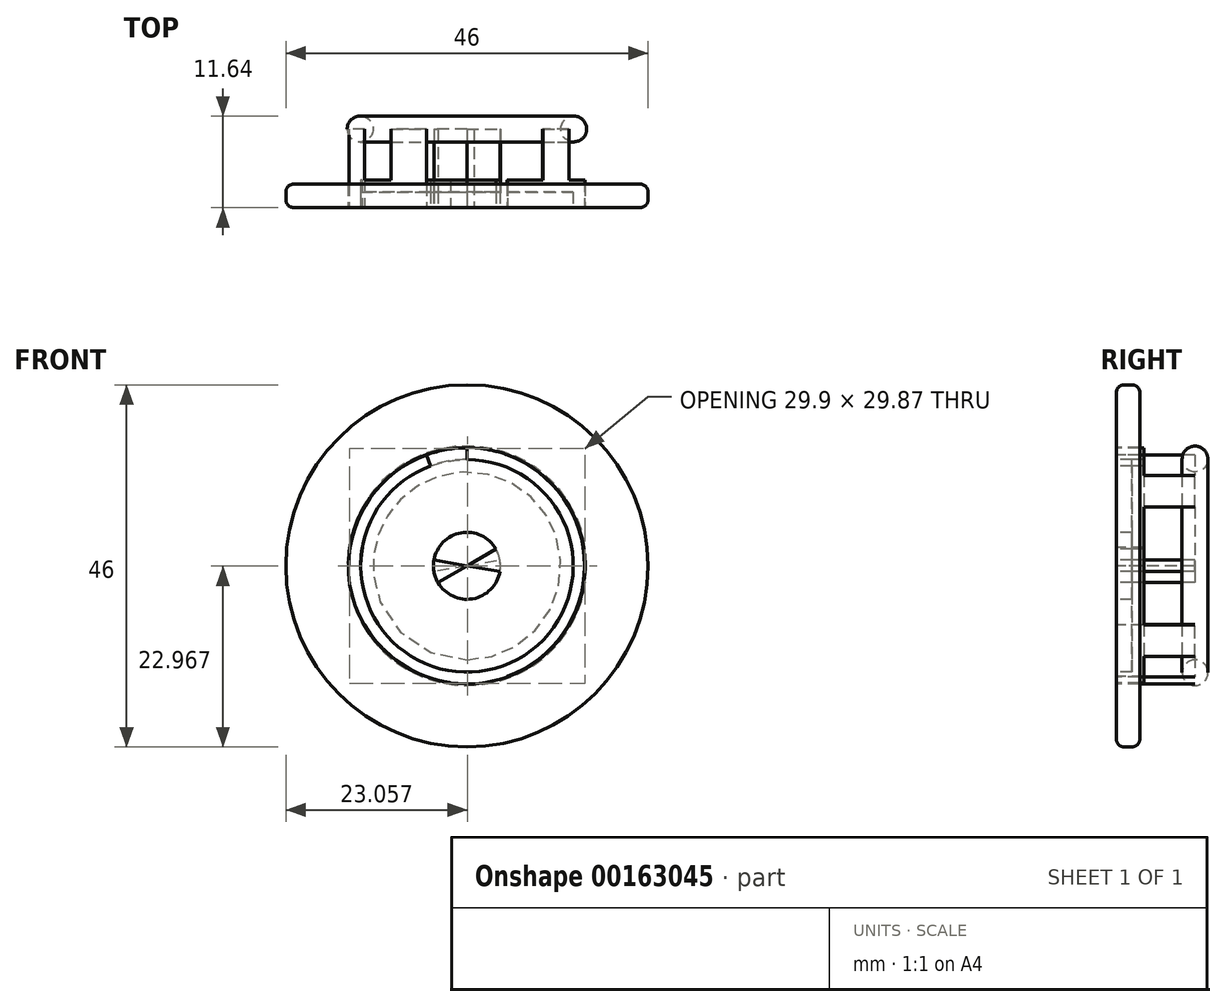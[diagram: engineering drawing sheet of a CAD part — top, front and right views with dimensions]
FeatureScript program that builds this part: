
annotation { "Feature Type Name" : "Feature", "Feature Type Description" : "" }
export const myFeature = defineFeature(function(context is Context, id is Id, definition is map)
    precondition{}
    {
        {
            var Q0;
            Q0=qCreatedBy(makeId("Front.planeOp"),FACE);
            var sketch = newSketch(context, id + "F0", { "sketchPlane" : qUnion([Q0])});
            skCircle(sketch, "E0", {"center": v(0, 0) * mm, "radius": 15 * mm});
            skCircle(sketch, "E1", {"center": v(0, 0) * mm, "radius": 4.25 * mm});
            skCircle(sketch, "E2", {"center": v(0, 0) * mm, "radius": 23 * mm});
            skCircle(sketch, "E3", {"center": v(0, 0) * mm, "radius": 13.5 * mm});
            skLineSegment(sketch, "E4", {"start": v(0, 0) * mm, "end": v(0, 15) * mm});
            skLineSegment(sketch, "E5.1.0", {"start": v(0, 0) * mm, "end": v(-5.13, 14.1) * mm});
            skLineSegment(sketch, "E5.2.0", {"start": v(0, 0) * mm, "end": v(-9.64, 11.5) * mm});
            skLineSegment(sketch, "E6.1.3.0", {"start": v(0, 0) * mm, "end": v(-13, 7.5) * mm});
            skArc(sketch, "E6.3.3.0", {"start": v(0, 13.5) * mm, "mid": v(-2.34, -13.3) * mm, "end": v(4.62, 12.69) * mm});
            skLineSegment(sketch, "E6.1.4.0", {"start": v(0, 0) * mm, "end": v(-14.77, 2.6) * mm});
            skArc(sketch, "E6.5.4.0", {"start": v(1.74, 14.9) * mm, "mid": v(-2.17, -14.84) * mm, "end": v(2.6, 14.77) * mm});
            skLineSegment(sketch, "E6.1.5.0", {"start": v(0, 0) * mm, "end": v(-14.77, -2.6) * mm});
            skArc(sketch, "E6.3.5.0", {"start": v(0, 13.5) * mm, "mid": v(-6.75, -11.7) * mm, "end": v(11.7, 6.75) * mm});
            skLineSegment(sketch, "E6.1.6.0", {"start": v(0, 0) * mm, "end": v(-13, -7.5) * mm});
            skLineSegment(sketch, "E6.1.7.0", {"start": v(0, 0) * mm, "end": v(-9.64, -11.5) * mm});
            skArc(sketch, "E6.3.7.0", {"start": v(0, 13.5) * mm, "mid": v(-2.34, -13.3) * mm, "end": v(4.62, 12.69) * mm});
            skArc(sketch, "E6.5.7.0", {"start": v(0, 15) * mm, "mid": v(-2.6, -14.77) * mm, "end": v(5.13, 14.1) * mm});
            skLineSegment(sketch, "E6.1.8.0", {"start": v(0, 0) * mm, "end": v(-5.13, -14.1) * mm});
            skLineSegment(sketch, "E7.1.9.0", {"start": v(0, 0) * mm, "end": v(0, -15) * mm});
            skLineSegment(sketch, "E7.1.10.0", {"start": v(0, 0) * mm, "end": v(5.13, -14.1) * mm});
            skArc(sketch, "E7.5.10.0", {"start": v(0, 15) * mm, "mid": v(-7.5, -13) * mm, "end": v(13, 7.5) * mm});
            skLineSegment(sketch, "E7.1.11.0", {"start": v(0, 0) * mm, "end": v(9.64, -11.5) * mm});
            skLineSegment(sketch, "E7.1.12.0", {"start": v(0, 0) * mm, "end": v(13, -7.5) * mm});
            skLineSegment(sketch, "E7.1.13.0", {"start": v(0, 0) * mm, "end": v(14.77, -2.6) * mm});
            skLineSegment(sketch, "E7.1.14.0", {"start": v(0, 0) * mm, "end": v(14.77, 2.6) * mm});
            skLineSegment(sketch, "E7.1.15.0", {"start": v(0, 0) * mm, "end": v(13, 7.5) * mm});
            skLineSegment(sketch, "E7.1.16.0", {"start": v(0, 0) * mm, "end": v(9.64, 11.5) * mm});
            skLineSegment(sketch, "E7.1.17.0", {"start": v(0, 0) * mm, "end": v(5.13, 14.1) * mm});
            skArc(sketch, "E8.trimOffspring", {"start": v(8.68, 10.34) * mm, "mid": v(6.75, 11.7) * mm, "end": v(4.62, 12.69) * mm});
            skArc(sketch, "E9.trimOffspring", {"start": v(9.64, 11.5) * mm, "mid": v(7.5, 13) * mm, "end": v(5.13, 14.1) * mm});
            skArc(sketch, "E10", {"start": v(1.74, 14.9) * mm, "mid": v(0.87, 14.97) * mm, "end": v(0, 15) * mm});
            skArc(sketch, "E11", {"start": v(5.13, 14.1) * mm, "mid": v(3.46, 14.6) * mm, "end": v(1.74, 14.9) * mm});
            skLineSegment(sketch, "E12", {"start": v(1.74, 14.9) * mm, "end": v(1.74, 14.9) * mm});
            skArc(sketch, "E13", {"start": v(13, 7.5) * mm, "mid": v(11.5, 9.64) * mm, "end": v(9.64, 11.5) * mm});
            skPoint(sketch, "E14.orphan", {"position": v(-26.97, -15.57) * mm});
            skPoint(sketch, "E15.orphan", {"position": v(-20.02, -23.86) * mm});
            skPoint(sketch, "E16.orphan", {"position": v(-10.65, -29.27) * mm});
            skPoint(sketch, "E17.orphan", {"position": v(0, -31.14) * mm});
            skPoint(sketch, "E18.orphan", {"position": v(10.65, -29.27) * mm});
            skPoint(sketch, "E19.orphan", {"position": v(20.02, -23.86) * mm});
            skPoint(sketch, "E20.orphan", {"position": v(26.97, -15.57) * mm});
            skSolve(sketch);
        }
        {
            var Q0;
            {var subQ0=sQuery(id+"F0.wireOp",EDGE,"E0");var subQ1=sQuery(id+"F0.wireOp",EDGE,"E5.1.0");var subQ2=makeQuery(id+"F0.imprint","INTERSECT",VERTEX,{"derivedFrom":[subQ1,subQ0]});Q0=makeQuery(id+"F0.imprint","IMPRINT",FACE,{"disambiguationData":[TD([[makeQuery(id+"F0.imprint","IMPRINT",EDGE,{"disambiguationData":[TD([[subQ2,1.0]])],"derivedFrom":subQ1}),1.0]])]});}
            var Q1;
            {var subQ0=sQuery(id+"F0.wireOp",EDGE,"E0");var subQ6=makeQuery(id+"F0.imprint","IMPRINT",VERTEX,{"disambiguationData":[OD(0.0)],"derivedFrom":subQ0});Q1=makeQuery(id+"F0.imprint","IMPRINT",FACE,{"disambiguationData":[TD([[makeQuery(id+"F0.imprint","IMPRINT",EDGE,{"disambiguationData":[TD([[subQ6,-1.0]])],"derivedFrom":subQ0}),1.0]])]});}
            var Q2;
            {var subQ0=sQuery(id+"F0.wireOp",EDGE,"E0");var subQ1=sQuery(id+"F0.wireOp",EDGE,"E7.1.15.0");var subQ2=makeQuery(id+"F0.imprint","INTERSECT",VERTEX,{"derivedFrom":[subQ1,subQ0]});Q2=makeQuery(id+"F0.imprint","IMPRINT",FACE,{"disambiguationData":[TD([[makeQuery(id+"F0.imprint","IMPRINT",EDGE,{"disambiguationData":[TD([[subQ2,1.0]])],"derivedFrom":subQ1}),1.0]])]});}
            var Q3;
            {var subQ0=sQuery(id+"F0.wireOp",EDGE,"E0");var subQ1=sQuery(id+"F0.wireOp",EDGE,"E7.1.13.0");var subQ2=makeQuery(id+"F0.imprint","INTERSECT",VERTEX,{"derivedFrom":[subQ1,subQ0]});Q3=makeQuery(id+"F0.imprint","IMPRINT",FACE,{"disambiguationData":[TD([[makeQuery(id+"F0.imprint","IMPRINT",EDGE,{"disambiguationData":[TD([[subQ2,1.0]])],"derivedFrom":subQ1}),1.0]])]});}
            var Q4;
            {var subQ0=sQuery(id+"F0.wireOp",EDGE,"E0");var subQ1=sQuery(id+"F0.wireOp",EDGE,"E7.1.11.0");var subQ2=makeQuery(id+"F0.imprint","INTERSECT",VERTEX,{"derivedFrom":[subQ1,subQ0]});Q4=makeQuery(id+"F0.imprint","IMPRINT",FACE,{"disambiguationData":[TD([[makeQuery(id+"F0.imprint","IMPRINT",EDGE,{"disambiguationData":[TD([[subQ2,1.0]])],"derivedFrom":subQ1}),1.0]])]});}
            var Q5;
            {var subQ0=sQuery(id+"F0.wireOp",EDGE,"E0");var subQ1=sQuery(id+"F0.wireOp",EDGE,"E7.1.9.0");var subQ2=makeQuery(id+"F0.imprint","INTERSECT",VERTEX,{"derivedFrom":[subQ1,subQ0]});Q5=makeQuery(id+"F0.imprint","IMPRINT",FACE,{"disambiguationData":[TD([[makeQuery(id+"F0.imprint","IMPRINT",EDGE,{"disambiguationData":[TD([[subQ2,1.0]])],"derivedFrom":subQ1}),1.0]])]});}
            var Q6;
            {var subQ0=sQuery(id+"F0.wireOp",EDGE,"E0");var subQ1=sQuery(id+"F0.wireOp",EDGE,"E6.1.3.0");var subQ2=makeQuery(id+"F0.imprint","INTERSECT",VERTEX,{"derivedFrom":[subQ1,subQ0]});Q6=makeQuery(id+"F0.imprint","IMPRINT",FACE,{"disambiguationData":[TD([[makeQuery(id+"F0.imprint","IMPRINT",EDGE,{"disambiguationData":[TD([[subQ2,1.0]])],"derivedFrom":subQ1}),1.0]])]});}
            var Q7;
            {var subQ0=sQuery(id+"F0.wireOp",EDGE,"E0");var subQ1=sQuery(id+"F0.wireOp",EDGE,"E6.1.5.0");var subQ2=makeQuery(id+"F0.imprint","INTERSECT",VERTEX,{"derivedFrom":[subQ1,subQ0]});Q7=makeQuery(id+"F0.imprint","IMPRINT",FACE,{"disambiguationData":[TD([[makeQuery(id+"F0.imprint","IMPRINT",EDGE,{"disambiguationData":[TD([[subQ2,1.0]])],"derivedFrom":subQ1}),1.0]])]});}
            var Q8;
            {var subQ0=sQuery(id+"F0.wireOp",EDGE,"E0");var subQ1=sQuery(id+"F0.wireOp",EDGE,"E6.1.7.0");var subQ2=makeQuery(id+"F0.imprint","INTERSECT",VERTEX,{"derivedFrom":[subQ1,subQ0]});Q8=makeQuery(id+"F0.imprint","IMPRINT",FACE,{"disambiguationData":[TD([[makeQuery(id+"F0.imprint","IMPRINT",EDGE,{"disambiguationData":[TD([[subQ2,1.0]])],"derivedFrom":subQ1}),1.0]])]});}
            extrude(context, id + "F1", {"entities" : qUnion([Q0, Q1, Q2, Q3, Q4, Q5, Q6, Q7, Q8]), "oppositeDirection" : true, "depth" : 10 * mm});
        }
        {
            var Q0;
            {var subQ0=sQuery(id+"F0.wireOp",EDGE,"E4");var subQ1=sQuery(id+"F0.wireOp",EDGE,"E1");var subQ2=makeQuery(id+"F0.imprint","INTERSECT",VERTEX,{"derivedFrom":[subQ1,subQ0]});Q0=makeQuery(id+"F0.imprint","IMPRINT",FACE,{"disambiguationData":[TD([[makeQuery(id+"F0.imprint","IMPRINT",EDGE,{"disambiguationData":[TD([[subQ2,-1.0]])],"derivedFrom":subQ1}),-1.0]])]});}
            var Q1;
            {var subQ0=sQuery(id+"F0.wireOp",EDGE,"E7.1.17.0");var subQ1=sQuery(id+"F0.wireOp",EDGE,"E1");var subQ2=makeQuery(id+"F0.imprint","INTERSECT",VERTEX,{"derivedFrom":[subQ1,subQ0]});Q1=makeQuery(id+"F0.imprint","IMPRINT",FACE,{"disambiguationData":[TD([[makeQuery(id+"F0.imprint","IMPRINT",EDGE,{"disambiguationData":[TD([[subQ2,-1.0]])],"derivedFrom":subQ1}),-1.0]])]});}
            var Q2;
            {var subQ0=sQuery(id+"F0.wireOp",EDGE,"E7.1.16.0");var subQ1=sQuery(id+"F0.wireOp",EDGE,"E1");var subQ2=makeQuery(id+"F0.imprint","INTERSECT",VERTEX,{"derivedFrom":[subQ1,subQ0]});Q2=makeQuery(id+"F0.imprint","IMPRINT",FACE,{"disambiguationData":[TD([[makeQuery(id+"F0.imprint","IMPRINT",EDGE,{"disambiguationData":[TD([[subQ2,-1.0]])],"derivedFrom":subQ1}),-1.0]])]});}
            var Q3;
            {var subQ0=sQuery(id+"F0.wireOp",EDGE,"E7.1.15.0");var subQ1=sQuery(id+"F0.wireOp",EDGE,"E1");var subQ2=makeQuery(id+"F0.imprint","INTERSECT",VERTEX,{"derivedFrom":[subQ1,subQ0]});Q3=makeQuery(id+"F0.imprint","IMPRINT",FACE,{"disambiguationData":[TD([[makeQuery(id+"F0.imprint","IMPRINT",EDGE,{"disambiguationData":[TD([[subQ2,-1.0]])],"derivedFrom":subQ1}),-1.0]])]});}
            var Q4;
            {var subQ0=sQuery(id+"F0.wireOp",EDGE,"E7.1.15.0");var subQ1=sQuery(id+"F0.wireOp",EDGE,"E1");var subQ2=makeQuery(id+"F0.imprint","INTERSECT",VERTEX,{"derivedFrom":[subQ1,subQ0]});Q4=makeQuery(id+"F0.imprint","IMPRINT",FACE,{"disambiguationData":[TD([[makeQuery(id+"F0.imprint","IMPRINT",EDGE,{"disambiguationData":[TD([[subQ2,1.0]])],"derivedFrom":subQ1}),-1.0]])]});}
            var Q5;
            {var subQ0=sQuery(id+"F0.wireOp",EDGE,"E7.1.14.0");var subQ1=sQuery(id+"F0.wireOp",EDGE,"E1");var subQ2=makeQuery(id+"F0.imprint","INTERSECT",VERTEX,{"derivedFrom":[subQ1,subQ0]});Q5=makeQuery(id+"F0.imprint","IMPRINT",FACE,{"disambiguationData":[TD([[makeQuery(id+"F0.imprint","IMPRINT",EDGE,{"disambiguationData":[TD([[subQ2,1.0]])],"derivedFrom":subQ1}),-1.0]])]});}
            var Q6;
            {var subQ0=sQuery(id+"F0.wireOp",EDGE,"E7.1.12.0");var subQ1=sQuery(id+"F0.wireOp",EDGE,"E1");var subQ2=makeQuery(id+"F0.imprint","INTERSECT",VERTEX,{"derivedFrom":[subQ1,subQ0]});Q6=makeQuery(id+"F0.imprint","IMPRINT",FACE,{"disambiguationData":[TD([[makeQuery(id+"F0.imprint","IMPRINT",EDGE,{"disambiguationData":[TD([[subQ2,-1.0]])],"derivedFrom":subQ1}),-1.0]])]});}
            var Q7;
            {var subQ0=sQuery(id+"F0.wireOp",EDGE,"E7.1.11.0");var subQ1=sQuery(id+"F0.wireOp",EDGE,"E1");var subQ2=makeQuery(id+"F0.imprint","INTERSECT",VERTEX,{"derivedFrom":[subQ1,subQ0]});Q7=makeQuery(id+"F0.imprint","IMPRINT",FACE,{"disambiguationData":[TD([[makeQuery(id+"F0.imprint","IMPRINT",EDGE,{"disambiguationData":[TD([[subQ2,-1.0]])],"derivedFrom":subQ1}),-1.0]])]});}
            var Q8;
            {var subQ0=sQuery(id+"F0.wireOp",EDGE,"E7.1.10.0");var subQ1=sQuery(id+"F0.wireOp",EDGE,"E1");var subQ2=makeQuery(id+"F0.imprint","INTERSECT",VERTEX,{"derivedFrom":[subQ1,subQ0]});Q8=makeQuery(id+"F0.imprint","IMPRINT",FACE,{"disambiguationData":[TD([[makeQuery(id+"F0.imprint","IMPRINT",EDGE,{"disambiguationData":[TD([[subQ2,-1.0]])],"derivedFrom":subQ1}),-1.0]])]});}
            var Q9;
            {var subQ0=sQuery(id+"F0.wireOp",EDGE,"E7.1.9.0");var subQ1=sQuery(id+"F0.wireOp",EDGE,"E1");var subQ2=makeQuery(id+"F0.imprint","INTERSECT",VERTEX,{"derivedFrom":[subQ1,subQ0]});Q9=makeQuery(id+"F0.imprint","IMPRINT",FACE,{"disambiguationData":[TD([[makeQuery(id+"F0.imprint","IMPRINT",EDGE,{"disambiguationData":[TD([[subQ2,-1.0]])],"derivedFrom":subQ1}),-1.0]])]});}
            var Q10;
            {var subQ0=sQuery(id+"F0.wireOp",EDGE,"E6.1.8.0");var subQ1=sQuery(id+"F0.wireOp",EDGE,"E1");var subQ2=makeQuery(id+"F0.imprint","INTERSECT",VERTEX,{"derivedFrom":[subQ1,subQ0]});Q10=makeQuery(id+"F0.imprint","IMPRINT",FACE,{"disambiguationData":[TD([[makeQuery(id+"F0.imprint","IMPRINT",EDGE,{"disambiguationData":[TD([[subQ2,-1.0]])],"derivedFrom":subQ1}),-1.0]])]});}
            var Q11;
            {var subQ0=sQuery(id+"F0.wireOp",EDGE,"E6.1.7.0");var subQ1=sQuery(id+"F0.wireOp",EDGE,"E1");var subQ2=makeQuery(id+"F0.imprint","INTERSECT",VERTEX,{"derivedFrom":[subQ1,subQ0]});Q11=makeQuery(id+"F0.imprint","IMPRINT",FACE,{"disambiguationData":[TD([[makeQuery(id+"F0.imprint","IMPRINT",EDGE,{"disambiguationData":[TD([[subQ2,-1.0]])],"derivedFrom":subQ1}),-1.0]])]});}
            var Q12;
            {var subQ0=sQuery(id+"F0.wireOp",EDGE,"E6.1.6.0");var subQ1=sQuery(id+"F0.wireOp",EDGE,"E1");var subQ2=makeQuery(id+"F0.imprint","INTERSECT",VERTEX,{"derivedFrom":[subQ1,subQ0]});Q12=makeQuery(id+"F0.imprint","IMPRINT",FACE,{"disambiguationData":[TD([[makeQuery(id+"F0.imprint","IMPRINT",EDGE,{"disambiguationData":[TD([[subQ2,-1.0]])],"derivedFrom":subQ1}),-1.0]])]});}
            var Q13;
            {var subQ0=sQuery(id+"F0.wireOp",EDGE,"E6.1.5.0");var subQ1=sQuery(id+"F0.wireOp",EDGE,"E1");var subQ2=makeQuery(id+"F0.imprint","INTERSECT",VERTEX,{"derivedFrom":[subQ1,subQ0]});Q13=makeQuery(id+"F0.imprint","IMPRINT",FACE,{"disambiguationData":[TD([[makeQuery(id+"F0.imprint","IMPRINT",EDGE,{"disambiguationData":[TD([[subQ2,-1.0]])],"derivedFrom":subQ1}),-1.0]])]});}
            var Q14;
            {var subQ0=sQuery(id+"F0.wireOp",EDGE,"E6.1.4.0");var subQ1=sQuery(id+"F0.wireOp",EDGE,"E1");var subQ2=makeQuery(id+"F0.imprint","INTERSECT",VERTEX,{"derivedFrom":[subQ1,subQ0]});Q14=makeQuery(id+"F0.imprint","IMPRINT",FACE,{"disambiguationData":[TD([[makeQuery(id+"F0.imprint","IMPRINT",EDGE,{"disambiguationData":[TD([[subQ2,-1.0]])],"derivedFrom":subQ1}),-1.0]])]});}
            var Q15;
            {var subQ0=sQuery(id+"F0.wireOp",EDGE,"E6.1.3.0");var subQ1=sQuery(id+"F0.wireOp",EDGE,"E1");var subQ2=makeQuery(id+"F0.imprint","INTERSECT",VERTEX,{"derivedFrom":[subQ1,subQ0]});Q15=makeQuery(id+"F0.imprint","IMPRINT",FACE,{"disambiguationData":[TD([[makeQuery(id+"F0.imprint","IMPRINT",EDGE,{"disambiguationData":[TD([[subQ2,-1.0]])],"derivedFrom":subQ1}),-1.0]])]});}
            var Q16;
            {var subQ0=sQuery(id+"F0.wireOp",EDGE,"E5.2.0");var subQ1=sQuery(id+"F0.wireOp",EDGE,"E1");var subQ2=makeQuery(id+"F0.imprint","INTERSECT",VERTEX,{"derivedFrom":[subQ1,subQ0]});Q16=makeQuery(id+"F0.imprint","IMPRINT",FACE,{"disambiguationData":[TD([[makeQuery(id+"F0.imprint","IMPRINT",EDGE,{"disambiguationData":[TD([[subQ2,-1.0]])],"derivedFrom":subQ1}),-1.0]])]});}
            var Q17;
            {var subQ0=sQuery(id+"F0.wireOp",EDGE,"E5.1.0");var subQ1=sQuery(id+"F0.wireOp",EDGE,"E1");var subQ2=makeQuery(id+"F0.imprint","INTERSECT",VERTEX,{"derivedFrom":[subQ1,subQ0]});Q17=makeQuery(id+"F0.imprint","IMPRINT",FACE,{"disambiguationData":[TD([[makeQuery(id+"F0.imprint","IMPRINT",EDGE,{"disambiguationData":[TD([[subQ2,-1.0]])],"derivedFrom":subQ1}),-1.0]])]});}
            extrude(context, id + "F2", {"entities" : qUnion([Q0, Q1, Q2, Q3, Q4, Q5, Q6, Q7, Q8, Q9, Q10, Q11, Q12, Q13, Q14, Q15, Q16, Q17]), "oppositeDirection" : true, "depth" : 2 * mm});
        }
        {
            var Q0;
            Q0=makeQuery(id+"F0.imprint","IMPRINT",FACE,{"disambiguationData":[TD([[makeQuery(id+"F0.imprint","IMPRINT",EDGE,{"derivedFrom":sQuery(id+"F0.wireOp",EDGE,"E2")}),1.0]])]});
            extrude(context, id + "F3", {"entities" : qUnion([Q0]), "oppositeDirection" : true, "depth" : 3 * mm});
        }
        {
            var Q0;
            {var subQ0=sQuery(id+"F0.wireOp",EDGE,"E0");var subQ1=sQuery(id+"F0.wireOp",EDGE,"E6.1.4.0");var subQ2=makeQuery(id+"F0.imprint","INTERSECT",VERTEX,{"derivedFrom":[subQ1,subQ0]});Q0=makeQuery(id+"F0.imprint","IMPRINT",FACE,{"disambiguationData":[TD([[makeQuery(id+"F0.imprint","IMPRINT",EDGE,{"disambiguationData":[TD([[subQ2,1.0]])],"derivedFrom":subQ1}),1.0]])]});}
            var Q1;
            {var subQ0=sQuery(id+"F0.wireOp",EDGE,"E0");var subQ1=sQuery(id+"F0.wireOp",EDGE,"E5.2.0");var subQ2=makeQuery(id+"F0.imprint","INTERSECT",VERTEX,{"derivedFrom":[subQ1,subQ0]});Q1=makeQuery(id+"F0.imprint","IMPRINT",FACE,{"disambiguationData":[TD([[makeQuery(id+"F0.imprint","IMPRINT",EDGE,{"disambiguationData":[TD([[subQ2,1.0]])],"derivedFrom":subQ1}),1.0]])]});}
            var Q2;
            {var subQ0=sQuery(id+"F0.wireOp",EDGE,"E0");var subQ1=sQuery(id+"F0.wireOp",EDGE,"E4");var subQ2=makeQuery(id+"F0.imprint","INTERSECT",VERTEX,{"derivedFrom":[subQ1,subQ0]});Q2=makeQuery(id+"F0.imprint","IMPRINT",FACE,{"disambiguationData":[TD([[makeQuery(id+"F0.imprint","IMPRINT",EDGE,{"disambiguationData":[TD([[subQ2,1.0]])],"derivedFrom":subQ1}),1.0]])]});}
            var Q3;
            {var subQ0=sQuery(id+"F0.wireOp",EDGE,"E0");var subQ1=sQuery(id+"F0.wireOp",EDGE,"E7.1.16.0");var subQ2=makeQuery(id+"F0.imprint","INTERSECT",VERTEX,{"derivedFrom":[subQ1,subQ0]});Q3=makeQuery(id+"F0.imprint","IMPRINT",FACE,{"disambiguationData":[TD([[makeQuery(id+"F0.imprint","IMPRINT",EDGE,{"disambiguationData":[TD([[subQ2,1.0]])],"derivedFrom":subQ1}),1.0]])]});}
            var Q4;
            {var subQ0=sQuery(id+"F0.wireOp",EDGE,"E0");var subQ1=sQuery(id+"F0.wireOp",EDGE,"E7.1.14.0");var subQ2=makeQuery(id+"F0.imprint","INTERSECT",VERTEX,{"derivedFrom":[subQ1,subQ0]});Q4=makeQuery(id+"F0.imprint","IMPRINT",FACE,{"disambiguationData":[TD([[makeQuery(id+"F0.imprint","IMPRINT",EDGE,{"disambiguationData":[TD([[subQ2,1.0]])],"derivedFrom":subQ1}),1.0]])]});}
            var Q5;
            {var subQ0=sQuery(id+"F0.wireOp",EDGE,"E0");var subQ1=sQuery(id+"F0.wireOp",EDGE,"E7.1.12.0");var subQ2=makeQuery(id+"F0.imprint","INTERSECT",VERTEX,{"derivedFrom":[subQ1,subQ0]});Q5=makeQuery(id+"F0.imprint","IMPRINT",FACE,{"disambiguationData":[TD([[makeQuery(id+"F0.imprint","IMPRINT",EDGE,{"disambiguationData":[TD([[subQ2,1.0]])],"derivedFrom":subQ1}),1.0]])]});}
            var Q6;
            {var subQ0=sQuery(id+"F0.wireOp",EDGE,"E0");var subQ1=sQuery(id+"F0.wireOp",EDGE,"E7.1.10.0");var subQ2=makeQuery(id+"F0.imprint","INTERSECT",VERTEX,{"derivedFrom":[subQ1,subQ0]});Q6=makeQuery(id+"F0.imprint","IMPRINT",FACE,{"disambiguationData":[TD([[makeQuery(id+"F0.imprint","IMPRINT",EDGE,{"disambiguationData":[TD([[subQ2,1.0]])],"derivedFrom":subQ1}),1.0]])]});}
            var Q7;
            {var subQ0=sQuery(id+"F0.wireOp",EDGE,"E0");var subQ1=sQuery(id+"F0.wireOp",EDGE,"E6.1.8.0");var subQ2=makeQuery(id+"F0.imprint","INTERSECT",VERTEX,{"derivedFrom":[subQ1,subQ0]});Q7=makeQuery(id+"F0.imprint","IMPRINT",FACE,{"disambiguationData":[TD([[makeQuery(id+"F0.imprint","IMPRINT",EDGE,{"disambiguationData":[TD([[subQ2,1.0]])],"derivedFrom":subQ1}),1.0]])]});}
            var Q8;
            {var subQ0=sQuery(id+"F0.wireOp",EDGE,"E0");var subQ1=sQuery(id+"F0.wireOp",EDGE,"E6.1.6.0");var subQ2=makeQuery(id+"F0.imprint","INTERSECT",VERTEX,{"derivedFrom":[subQ1,subQ0]});Q8=makeQuery(id+"F0.imprint","IMPRINT",FACE,{"disambiguationData":[TD([[makeQuery(id+"F0.imprint","IMPRINT",EDGE,{"disambiguationData":[TD([[subQ2,1.0]])],"derivedFrom":subQ1}),1.0]])]});}
            extrude(context, id + "F4", {"entities" : qUnion([Q0, Q1, Q2, Q3, Q4, Q5, Q6, Q7, Q8]), "operationType" : NewBodyOperationType.ADD, "oppositeDirection" : true, "depth" : 3.5 * mm});
        }
        {
            var Q0;
            Q0=qCreatedBy(makeId("Right.planeOp"),FACE);
            var sketch = newSketch(context, id + "F5", { "sketchPlane" : qUnion([Q0])});
            skCircle(sketch, "E21", {"center": v(10, -13.57) * mm, "radius": 1.64 * mm});
            skLineSegment(sketch, "E22", {"start": v(0, 0) * mm, "end": v(36.22, 0) * mm});
            skSolve(sketch);
        }
        {
            var Q0;
            Q0=makeQuery(id+"F5.imprint","IMPRINT",FACE,{"disambiguationData":[TD([[makeQuery(id+"F5.imprint","IMPRINT",EDGE,{"derivedFrom":sQuery(id+"F5.wireOp",EDGE,"E21")}),1.0]])]});
            var Q1;
            Q1=sQuery(id+"F5.wireOp",EDGE,"E22");
            revolve(context, id + "F6", {"entities" : qUnion([Q0]), "axis" : qUnion([Q1]), "revolveType" : RevolveType.FULL});
        }
        {
            var Q0;
            Q0=makeQuery(id+"F3.opExtrude","CAP_EDGE",EDGE,{"disambiguationData":[OSD([sQuery(id+"F0.wireOp",EDGE,"E2")])],"isStart":false});
            var Q1;
            Q1=makeQuery(id+"F3.opExtrude","CAP_EDGE",EDGE,{"disambiguationData":[OSD([sQuery(id+"F0.wireOp",EDGE,"E2")])],"isStart":true});
            fillet(context, id + "F7", {"entities" : qUnion([Q0, Q1]), "radius" : 1 * mm, "tangentPropagation" : true, "allowEdgeOverflow" : false});
        }
    });
